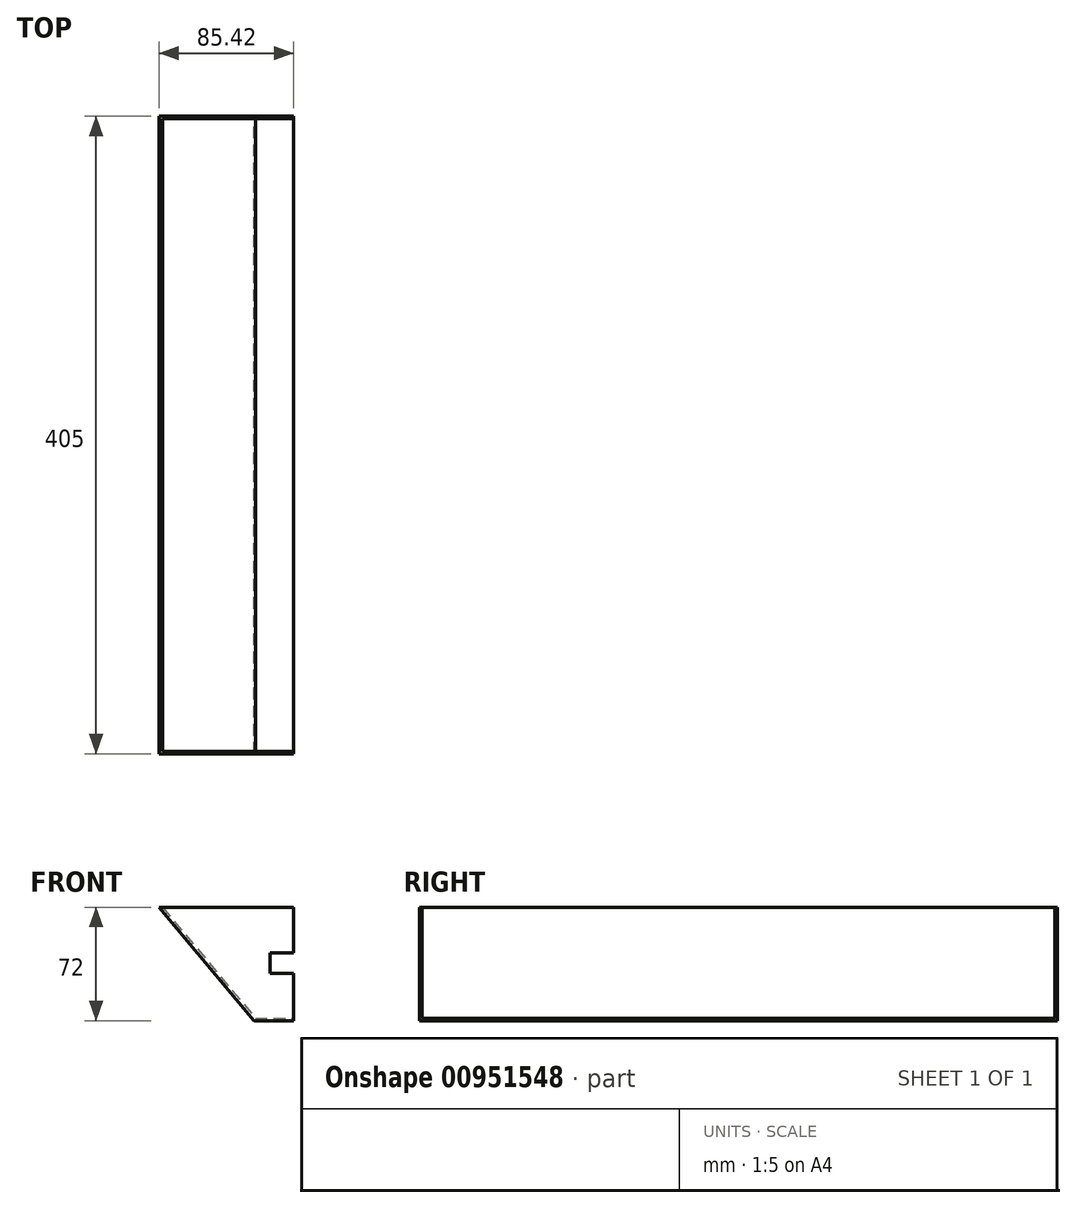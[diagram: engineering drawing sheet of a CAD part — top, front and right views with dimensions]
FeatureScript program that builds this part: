
annotation { "Feature Type Name" : "Feature", "Feature Type Description" : "" }
export const myFeature = defineFeature(function(context is Context, id is Id, definition is map)
    precondition{}
    {
        {
            var Q0;
            Q0=qCreatedBy(makeId("Front.planeOp"),FACE);
            var sketch = newSketch(context, id + "F0", { "sketchPlane" : qUnion([Q0])});
            skLineSegment(sketch, "E0", {"start": v(0, 0) * mm, "end": v(25, 0) * mm});
            skLineSegment(sketch, "E1", {"start": v(25, 0) * mm, "end": v(25, 30) * mm});
            skLineSegment(sketch, "E2", {"start": v(25, 30) * mm, "end": v(10, 30) * mm});
            skLineSegment(sketch, "E3", {"start": v(10, 30) * mm, "end": v(10, 43) * mm});
            skLineSegment(sketch, "E4", {"start": v(10, 43) * mm, "end": v(25, 43) * mm});
            skLineSegment(sketch, "E5", {"start": v(25, 43) * mm, "end": v(25, 72) * mm});
            skLineSegment(sketch, "E6", {"start": v(25, 72) * mm, "end": v(-60.42, 72) * mm});
            skLineSegment(sketch, "E7", {"start": v(-60.42, 72) * mm, "end": v(0, 0) * mm});
            skSolve(sketch);
        }
        {
            var Q0;
            Q0=makeQuery(id+"F0.imprint","IMPRINT",FACE,{"disambiguationData":[TD([[makeQuery(id+"F0.imprint","IMPRINT",EDGE,{"derivedFrom":sQuery(id+"F0.wireOp",EDGE,"E0")}),1.0]])]});
            extrude(context, id + "F1", {"entities" : qUnion([Q0]), "depth" : 405 * mm, "offsetDistance" : 25 * mm});
        }
        {
            var Q0;
            Q0=makeQuery(id+"F1.opExtrude","CAP_FACE",FACE,{"disambiguationData":[OSD([sQuery(id+"F0.wireOp",EDGE,"E0"),sQuery(id+"F0.wireOp",EDGE,"E1"),sQuery(id+"F0.wireOp",EDGE,"E2"),sQuery(id+"F0.wireOp",EDGE,"E3"),sQuery(id+"F0.wireOp",EDGE,"E4"),sQuery(id+"F0.wireOp",EDGE,"E5"),sQuery(id+"F0.wireOp",EDGE,"E6"),sQuery(id+"F0.wireOp",EDGE,"E7")])],"isStart":false});
            cPlane(context, id + "F2", {"entities" : qUnion([Q0]), "cplaneType" : CPlaneType.OFFSET, "offset" : 1.6 * mm, "oppositeDirection" : true, "width" : 150 * mm, "height" : 150 * mm});
        }
        {
            var Q0;
            Q0=qCreatedBy(id+"F2.planeOp",FACE);
            var sketch = newSketch(context, id + "F3", { "sketchPlane" : qUnion([Q0])});
            skLineSegment(sketch, "E8.0", {"start": v(-59.19, 73.03) * mm, "end": v(0.75, 1.6) * mm});
            skLineSegment(sketch, "E9.0", {"start": v(0.75, 1.6) * mm, "end": v(25, 1.6) * mm});
            skLineSegment(sketch, "E10", {"start": v(-59.19, 73.03) * mm, "end": v(29.36, 73.03) * mm});
            skLineSegment(sketch, "E11", {"start": v(29.36, 73.03) * mm, "end": v(25, 1.6) * mm});
            skSolve(sketch);
        }
        {
            var Q0;
            Q0=makeQuery(id+"F3.imprint","IMPRINT",FACE,{"disambiguationData":[TD([[makeQuery(id+"F3.imprint","IMPRINT",EDGE,{"derivedFrom":sQuery(id+"F3.wireOp",EDGE,"E8.0")}),1.0]])]});
            extrude(context, id + "F4", {"entities" : qUnion([Q0]), "operationType" : NewBodyOperationType.REMOVE, "oppositeDirection" : true, "depth" : 401.8 * mm, "offsetDistance" : 25 * mm});
        }
    });
